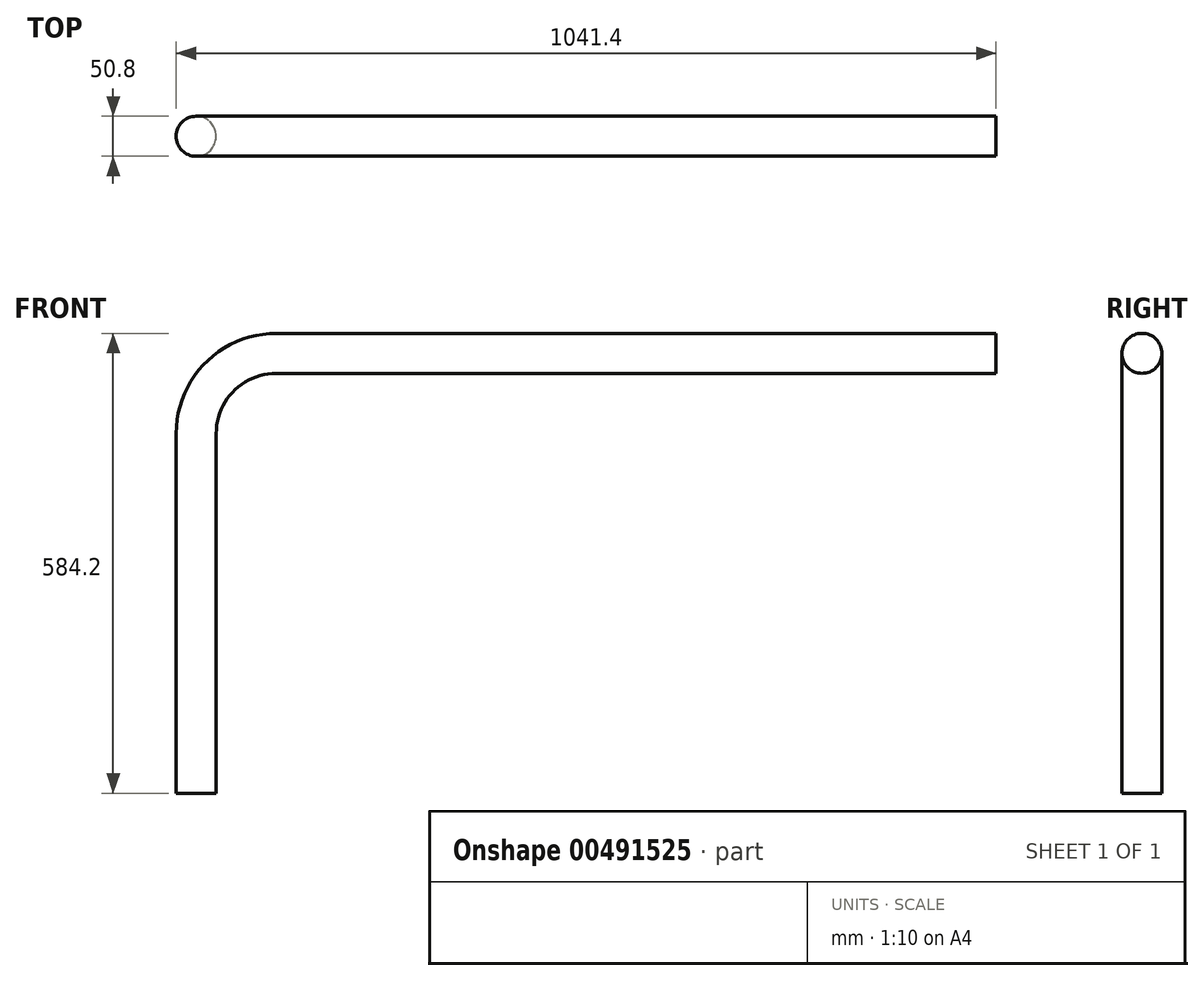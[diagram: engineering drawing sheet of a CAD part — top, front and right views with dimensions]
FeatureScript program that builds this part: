
annotation { "Feature Type Name" : "Feature", "Feature Type Description" : "" }
export const myFeature = defineFeature(function(context is Context, id is Id, definition is map)
    precondition{}
    {
        {
            var Q0;
            Q0=qCreatedBy(makeId("Front.planeOp"),FACE);
            var sketch = newSketch(context, id + "F0", { "sketchPlane" : qUnion([Q0])});
            skLineSegment(sketch, "E0", {"start": v(0, 0) * mm, "end": v(0, 457.2) * mm});
            skArc(sketch, "E1", {"start": v(76.2, 533.4) * mm, "mid": v(22.32, 511.08) * mm, "end": v(0, 457.2) * mm});
            skLineSegment(sketch, "E2", {"start": v(76.2, 533.4) * mm, "end": v(990.6, 533.4) * mm});
            skLineSegment(sketch, "E3.0", {"start": v(76.2, 584.2) * mm, "end": v(990.6, 584.2) * mm});
            skArc(sketch, "E3.1", {"start": v(76.2, 584.2) * mm, "mid": v(-13.6, 547) * mm, "end": v(-50.8, 457.2) * mm});
            skLineSegment(sketch, "E3.2", {"start": v(-50.8, 0) * mm, "end": v(-50.8, 457.2) * mm});
            skLineSegment(sketch, "E4", {"start": v(990.6, 584.2) * mm, "end": v(990.6, 533.4) * mm});
            skLineSegment(sketch, "E5", {"start": v(-50.8, 0) * mm, "end": v(0, 0) * mm});
            skSolve(sketch);
        }
        {
            var Q0;
            Q0=makeQuery(id+"F0.imprint","IMPRINT",FACE,{"disambiguationData":[TD([[makeQuery(id+"F0.imprint","IMPRINT",EDGE,{"derivedFrom":sQuery(id+"F0.wireOp",EDGE,"E0")}),1.0]])]});
            extrude(context, id + "F1", {"entities" : qUnion([Q0]), "endBound" : BoundingType.SYMMETRIC, "depth" : 50.8 * mm});
        }
        {
            var Q0;
            Q0=makeQuery(id+"F1.opExtrude","CAP_EDGE",EDGE,{"disambiguationData":[OSD([sQuery(id+"F0.wireOp",EDGE,"E3.0")])],"isStart":true});
            var Q1;
            Q1=makeQuery(id+"F1.opExtrude","CAP_EDGE",EDGE,{"disambiguationData":[OSD([sQuery(id+"F0.wireOp",EDGE,"E3.0")])],"isStart":false});
            var Q2;
            Q2=makeQuery(id+"F1.opExtrude","CAP_EDGE",EDGE,{"disambiguationData":[OSD([sQuery(id+"F0.wireOp",EDGE,"E2")])],"isStart":true});
            var Q3;
            Q3=makeQuery(id+"F1.opExtrude","CAP_EDGE",EDGE,{"disambiguationData":[OSD([sQuery(id+"F0.wireOp",EDGE,"E2")])],"isStart":false});
            var Q4;
            Q4=makeQuery(id+"F1.opExtrude","CAP_EDGE",EDGE,{"disambiguationData":[OSD([sQuery(id+"F0.wireOp",EDGE,"E3.1")])],"isStart":false});
            var Q5;
            Q5=makeQuery(id+"F1.opExtrude","CAP_EDGE",EDGE,{"disambiguationData":[OSD([sQuery(id+"F0.wireOp",EDGE,"E3.1")])],"isStart":true});
            var Q6;
            Q6=makeQuery(id+"F1.opExtrude","CAP_EDGE",EDGE,{"disambiguationData":[OSD([sQuery(id+"F0.wireOp",EDGE,"E1")])],"isStart":false});
            var Q7;
            Q7=makeQuery(id+"F1.opExtrude","CAP_EDGE",EDGE,{"disambiguationData":[OSD([sQuery(id+"F0.wireOp",EDGE,"E0")])],"isStart":false});
            var Q8;
            Q8=makeQuery(id+"F1.opExtrude","CAP_EDGE",EDGE,{"disambiguationData":[OSD([sQuery(id+"F0.wireOp",EDGE,"E3.2")])],"isStart":false});
            var Q9;
            Q9=makeQuery(id+"F1.opExtrude","CAP_EDGE",EDGE,{"disambiguationData":[OSD([sQuery(id+"F0.wireOp",EDGE,"E0")])],"isStart":true});
            var Q10;
            Q10=makeQuery(id+"F1.opExtrude","CAP_EDGE",EDGE,{"disambiguationData":[OSD([sQuery(id+"F0.wireOp",EDGE,"E3.2")])],"isStart":true});
            var Q11;
            Q11=makeQuery(id+"F1.opExtrude","CAP_EDGE",EDGE,{"disambiguationData":[OSD([sQuery(id+"F0.wireOp",EDGE,"E1")])],"isStart":true});
            fillet(context, id + "F2", {"entities" : qUnion([Q0, Q1, Q2, Q3, Q4, Q5, Q6, Q7, Q8, Q9, Q10, Q11]), "radius" : 25.4 * mm, "tangentPropagation" : true, "allowEdgeOverflow" : false});
        }
    });
